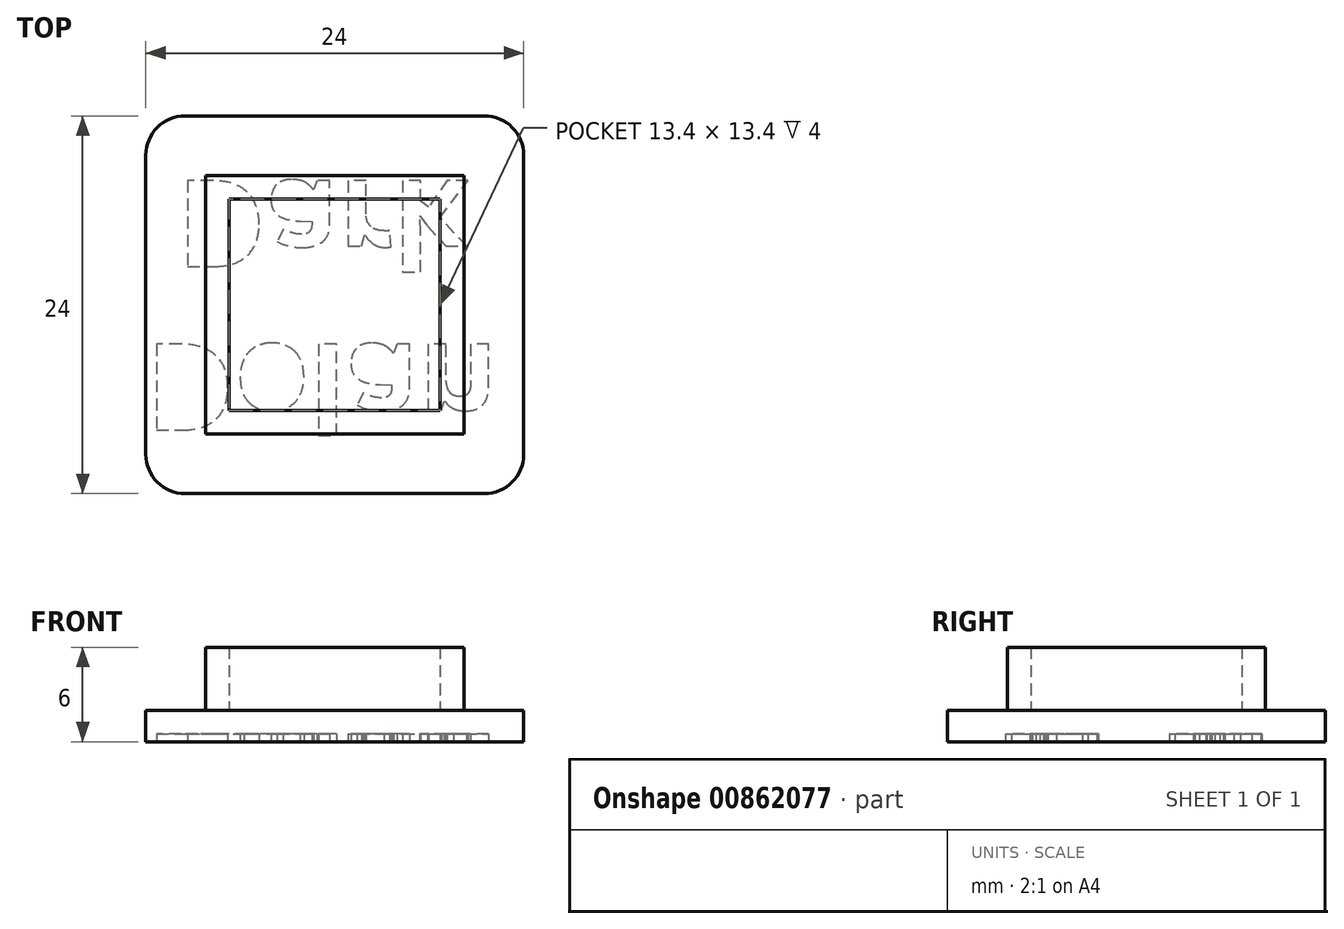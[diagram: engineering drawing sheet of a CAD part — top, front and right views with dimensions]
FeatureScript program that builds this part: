
annotation { "Feature Type Name" : "Feature", "Feature Type Description" : "" }
export const myFeature = defineFeature(function(context is Context, id is Id, definition is map)
    precondition{}
    {
        {
            var Q0;
            Q0=qCreatedBy(makeId("Top.planeOp"),FACE);
            var sketch = newSketch(context, id + "F0", { "sketchPlane" : qUnion([Q0])});
            skLineSegment(sketch, "E0.bottom", {"start": v(12, 12) * mm, "end": v(-12, 12) * mm});
            skLineSegment(sketch, "E0.top", {"start": v(12, -12) * mm, "end": v(-12, -12) * mm});
            skLineSegment(sketch, "E0.left", {"start": v(12, 12) * mm, "end": v(12, -12) * mm});
            skLineSegment(sketch, "E0.right", {"start": v(-12, 12) * mm, "end": v(-12, -12) * mm});
            skPoint(sketch, "E0.middle", {"position": v(0, 0) * mm});
            skSolve(sketch);
        }
        {
            var Q0;
            Q0=makeQuery(id+"F0.imprint","IMPRINT",FACE,{"disambiguationData":[TD([[makeQuery(id+"F0.imprint","IMPRINT",EDGE,{"derivedFrom":sQuery(id+"F0.wireOp",EDGE,"E0.bottom")}),1.0]])]});
            extrude(context, id + "F1", {"entities" : qUnion([Q0]), "depth" : 2 * mm, "offsetDistance" : 25 * mm});
        }
        {
            var Q0;
            Q0=makeQuery(id+"F1.opExtrude","CAP_FACE",FACE,{"disambiguationData":[OSD([sQuery(id+"F0.wireOp",EDGE,"E0.bottom"),sQuery(id+"F0.wireOp",EDGE,"E0.top"),sQuery(id+"F0.wireOp",EDGE,"E0.left"),sQuery(id+"F0.wireOp",EDGE,"E0.right")])],"isStart":false});
            var sketch = newSketch(context, id + "F2", { "sketchPlane" : qUnion([Q0])});
            skLineSegment(sketch, "E1.bottom", {"start": v(8.2, 8.2) * mm, "end": v(-8.2, 8.2) * mm});
            skLineSegment(sketch, "E1.top", {"start": v(8.2, -8.2) * mm, "end": v(-8.2, -8.2) * mm});
            skLineSegment(sketch, "E1.left", {"start": v(8.2, 8.2) * mm, "end": v(8.2, -8.2) * mm});
            skLineSegment(sketch, "E1.right", {"start": v(-8.2, 8.2) * mm, "end": v(-8.2, -8.2) * mm});
            skPoint(sketch, "E1.middle", {"position": v(0, 0) * mm});
            skLineSegment(sketch, "E2", {"start": v(-8.2, 0) * mm, "end": v(-6.7, 0) * mm});
            skLineSegment(sketch, "E3.bottom", {"start": v(6.7, -6.7) * mm, "end": v(-6.7, -6.7) * mm});
            skLineSegment(sketch, "E3.top", {"start": v(6.7, 6.7) * mm, "end": v(-6.7, 6.7) * mm});
            skLineSegment(sketch, "E3.left", {"start": v(6.7, -6.7) * mm, "end": v(6.7, 6.7) * mm});
            skLineSegment(sketch, "E3.right", {"start": v(-6.7, -6.7) * mm, "end": v(-6.7, 6.7) * mm});
            skSolve(sketch);
        }
        {
            var Q0;
            {var subQ1=sQuery(id+"F2.wireOp",EDGE,"E1.bottom");Q0=makeQuery(id+"F2.imprint","IMPRINT",FACE,{"disambiguationData":[TD([[makeQuery(id+"F2.imprint","IMPRINT",EDGE,{"derivedFrom":subQ1}),1.0]])]});}
            extrude(context, id + "F3", {"entities" : qUnion([Q0]), "operationType" : NewBodyOperationType.ADD, "depth" : 4 * mm, "offsetDistance" : 25 * mm});
        }
        {
            var Q0;
            Q0=makeQuery(id+"F1.opExtrude","SWEPT_EDGE",EDGE,{"disambiguationData":[OSD([sQuery(id+"F0.wireOp",EDGE,"E0.top"),sQuery(id+"F0.wireOp",EDGE,"E0.right")])]});
            var Q1;
            Q1=makeQuery(id+"F1.opExtrude","SWEPT_EDGE",EDGE,{"disambiguationData":[OSD([sQuery(id+"F0.wireOp",EDGE,"E0.bottom"),sQuery(id+"F0.wireOp",EDGE,"E0.right")])]});
            var Q2;
            Q2=makeQuery(id+"F1.opExtrude","SWEPT_EDGE",EDGE,{"disambiguationData":[OSD([sQuery(id+"F0.wireOp",EDGE,"E0.bottom"),sQuery(id+"F0.wireOp",EDGE,"E0.left")])]});
            var Q3;
            Q3=makeQuery(id+"F1.opExtrude","SWEPT_EDGE",EDGE,{"disambiguationData":[OSD([sQuery(id+"F0.wireOp",EDGE,"E0.top"),sQuery(id+"F0.wireOp",EDGE,"E0.left")])]});
            fillet(context, id + "F4", {"entities" : qUnion([Q0, Q1, Q2, Q3]), "radius" : 2.5 * mm, "tangentPropagation" : true, "allowEdgeOverflow" : false});
        }
        {
            var Q0;
            Q0=makeQuery(id+"F1.opExtrude","CAP_FACE",FACE,{"disambiguationData":[OSD([sQuery(id+"F0.wireOp",EDGE,"E0.bottom"),sQuery(id+"F0.wireOp",EDGE,"E0.top"),sQuery(id+"F0.wireOp",EDGE,"E0.left"),sQuery(id+"F0.wireOp",EDGE,"E0.right")])],"isStart":true});
            var sketch = newSketch(context, id + "F5", { "sketchPlane" : qUnion([Q0])});
            skLineSegment(sketch, "E4", {"start": v(-12, -9.5) * mm, "end": v(-12, 2.5) * mm});
            skText(sketch, "E5", { "text": "Dolan\n Dark", "fontName": "OpenSans-Bold.ttf"});
            const initialGuessF5  = {"E5": [-0.012, 0.0025, 1, 0, 0.0055]};
            skSetInitialGuess(sketch, initialGuessF5);
            skSolve(sketch);
        }
        {
            var Q0;
            Q0 = qSketchRegion(id + "F5", true);
            extrude(context, id + "F6", {"entities" : qUnion([Q0]), "operationType" : NewBodyOperationType.REMOVE, "oppositeDirection" : true, "depth" : .5 * mm, "offsetDistance" : 25 * mm});
        }
        {
            var Q0;
            Q0=makeQuery(id+"F6.boolean.opBoolean","SPLIT",FACE,{"disambiguationData":[TD([makeQuery(id+"F6.opExtrude","SWEPT_FACE",FACE,{"disambiguationData":[OSD([sQuery(id+"F5.wireOp",EDGE,"E5.sketch_text.stroke-7")])]})])],"derivedFrom":makeQuery(id+"F1.opExtrude","CAP_FACE",FACE,{"disambiguationData":[OSD([sQuery(id+"F0.wireOp",EDGE,"E0.bottom"),sQuery(id+"F0.wireOp",EDGE,"E0.top"),sQuery(id+"F0.wireOp",EDGE,"E0.left"),sQuery(id+"F0.wireOp",EDGE,"E0.right")])],"isStart":true})});
            var Q1;
            Q1=makeQuery(id+"F6.boolean.opBoolean","SPLIT",FACE,{"disambiguationData":[TD([makeQuery(id+"F6.opExtrude","SWEPT_FACE",FACE,{"disambiguationData":[OSD([sQuery(id+"F5.wireOp",EDGE,"E5.sketch_text.stroke-12")])]})])],"derivedFrom":makeQuery(id+"F1.opExtrude","CAP_FACE",FACE,{"disambiguationData":[OSD([sQuery(id+"F0.wireOp",EDGE,"E0.bottom"),sQuery(id+"F0.wireOp",EDGE,"E0.top"),sQuery(id+"F0.wireOp",EDGE,"E0.left"),sQuery(id+"F0.wireOp",EDGE,"E0.right")])],"isStart":true})});
            var Q2;
            Q2=makeQuery(id+"F6.boolean.opBoolean","SPLIT",FACE,{"disambiguationData":[TD([makeQuery(id+"F6.opExtrude","SWEPT_FACE",FACE,{"disambiguationData":[OSD([sQuery(id+"F5.wireOp",EDGE,"E5.sketch_text.stroke-83")])]})])],"derivedFrom":makeQuery(id+"F1.opExtrude","CAP_FACE",FACE,{"disambiguationData":[OSD([sQuery(id+"F0.wireOp",EDGE,"E0.bottom"),sQuery(id+"F0.wireOp",EDGE,"E0.top"),sQuery(id+"F0.wireOp",EDGE,"E0.left"),sQuery(id+"F0.wireOp",EDGE,"E0.right")])],"isStart":true})});
            var Q3;
            Q3=makeQuery(id+"F6.boolean.opBoolean","SPLIT",FACE,{"disambiguationData":[TD([makeQuery(id+"F6.opExtrude","SWEPT_FACE",FACE,{"disambiguationData":[OSD([sQuery(id+"F5.wireOp",EDGE,"E5.sketch_text.stroke-106")])]})])],"derivedFrom":makeQuery(id+"F1.opExtrude","CAP_FACE",FACE,{"disambiguationData":[OSD([sQuery(id+"F0.wireOp",EDGE,"E0.bottom"),sQuery(id+"F0.wireOp",EDGE,"E0.top"),sQuery(id+"F0.wireOp",EDGE,"E0.left"),sQuery(id+"F0.wireOp",EDGE,"E0.right")])],"isStart":true})});
            var Q4;
            Q4=makeQuery(id+"F6.boolean.opBoolean","SPLIT",FACE,{"disambiguationData":[TD([makeQuery(id+"F6.opExtrude","SWEPT_FACE",FACE,{"disambiguationData":[OSD([sQuery(id+"F5.wireOp",EDGE,"E5.sketch_text.stroke-52")])]})])],"derivedFrom":makeQuery(id+"F1.opExtrude","CAP_FACE",FACE,{"disambiguationData":[OSD([sQuery(id+"F0.wireOp",EDGE,"E0.bottom"),sQuery(id+"F0.wireOp",EDGE,"E0.top"),sQuery(id+"F0.wireOp",EDGE,"E0.left"),sQuery(id+"F0.wireOp",EDGE,"E0.right")])],"isStart":true})});
            extrude(context, id + "F7", {"entities" : qUnion([Q0, Q1, Q2, Q3, Q4]), "operationType" : NewBodyOperationType.REMOVE, "oppositeDirection" : true, "depth" : .5 * mm, "offsetDistance" : 25 * mm});
        }
    });
